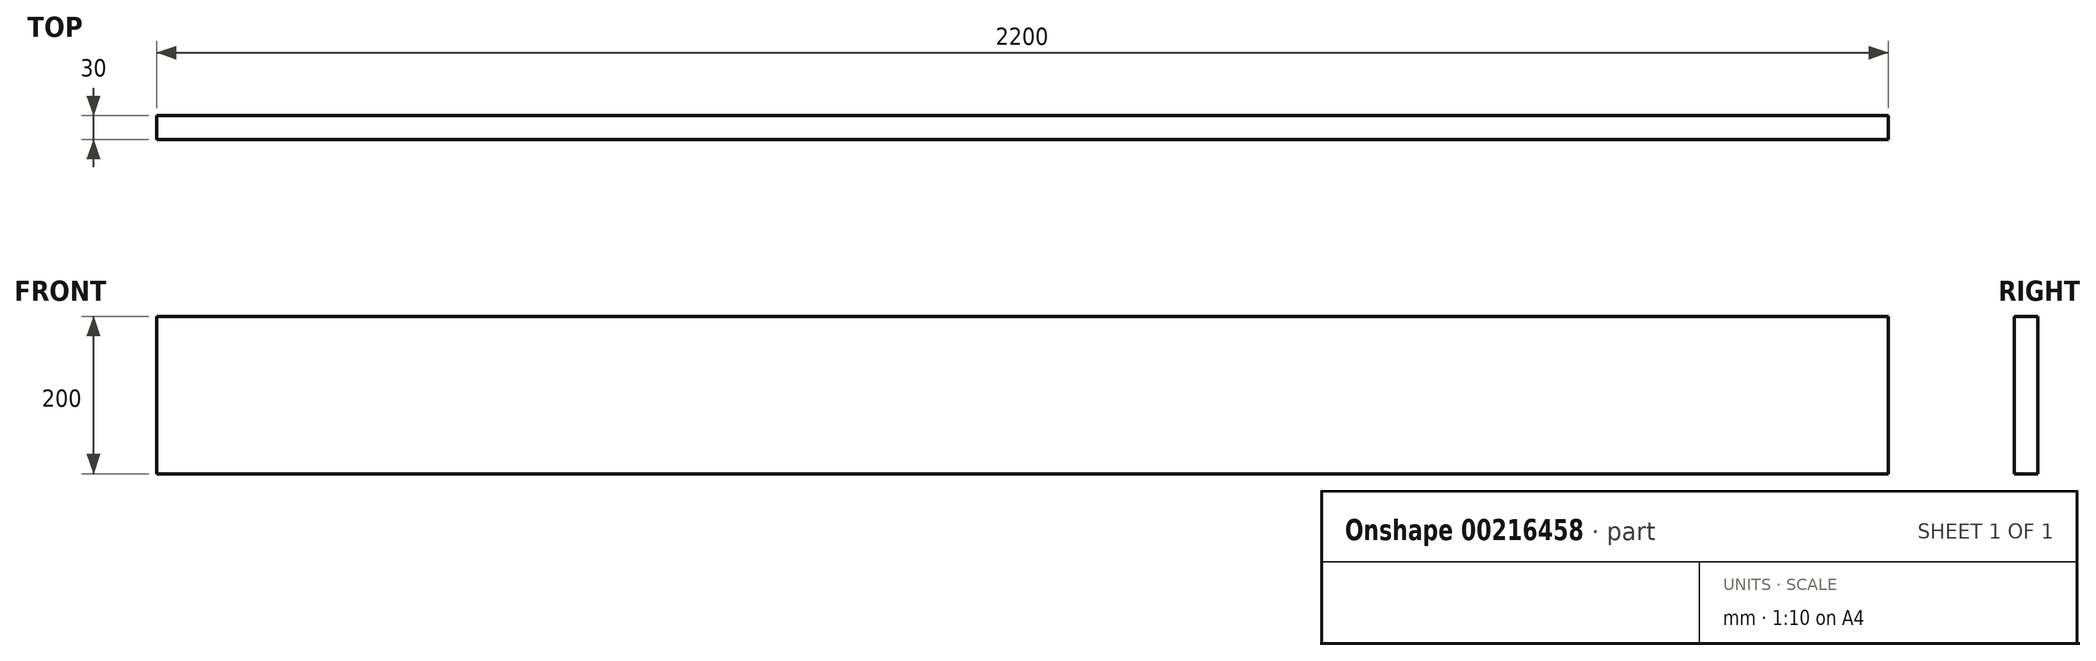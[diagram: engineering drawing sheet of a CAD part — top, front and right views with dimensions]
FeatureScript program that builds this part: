
annotation { "Feature Type Name" : "Feature", "Feature Type Description" : "" }
export const myFeature = defineFeature(function(context is Context, id is Id, definition is map)
    precondition{}
    {
        {
            var Q0;
            Q0=qCreatedBy(makeId("Right.planeOp"),FACE);
            var sketch = newSketch(context, id + "F0", { "sketchPlane" : qUnion([Q0])});
            skLineSegment(sketch, "E0.bottom", {"start": v(15, 100) * mm, "end": v(-15, 100) * mm});
            skLineSegment(sketch, "E0.top", {"start": v(15, -100) * mm, "end": v(-15, -100) * mm});
            skLineSegment(sketch, "E0.left", {"start": v(15, 100) * mm, "end": v(15, -100) * mm});
            skLineSegment(sketch, "E0.right", {"start": v(-15, 100) * mm, "end": v(-15, -100) * mm});
            skPoint(sketch, "E0.middle", {"position": v(0, 0) * mm});
            skSolve(sketch);
        }
        {
            var Q0;
            Q0 = qSketchRegion(id + "F0", true);
            extrude(context, id + "F1", {"entities" : qUnion([Q0]), "endBound" : BoundingType.SYMMETRIC, "depth" : 2200 * mm});
        }
    });
